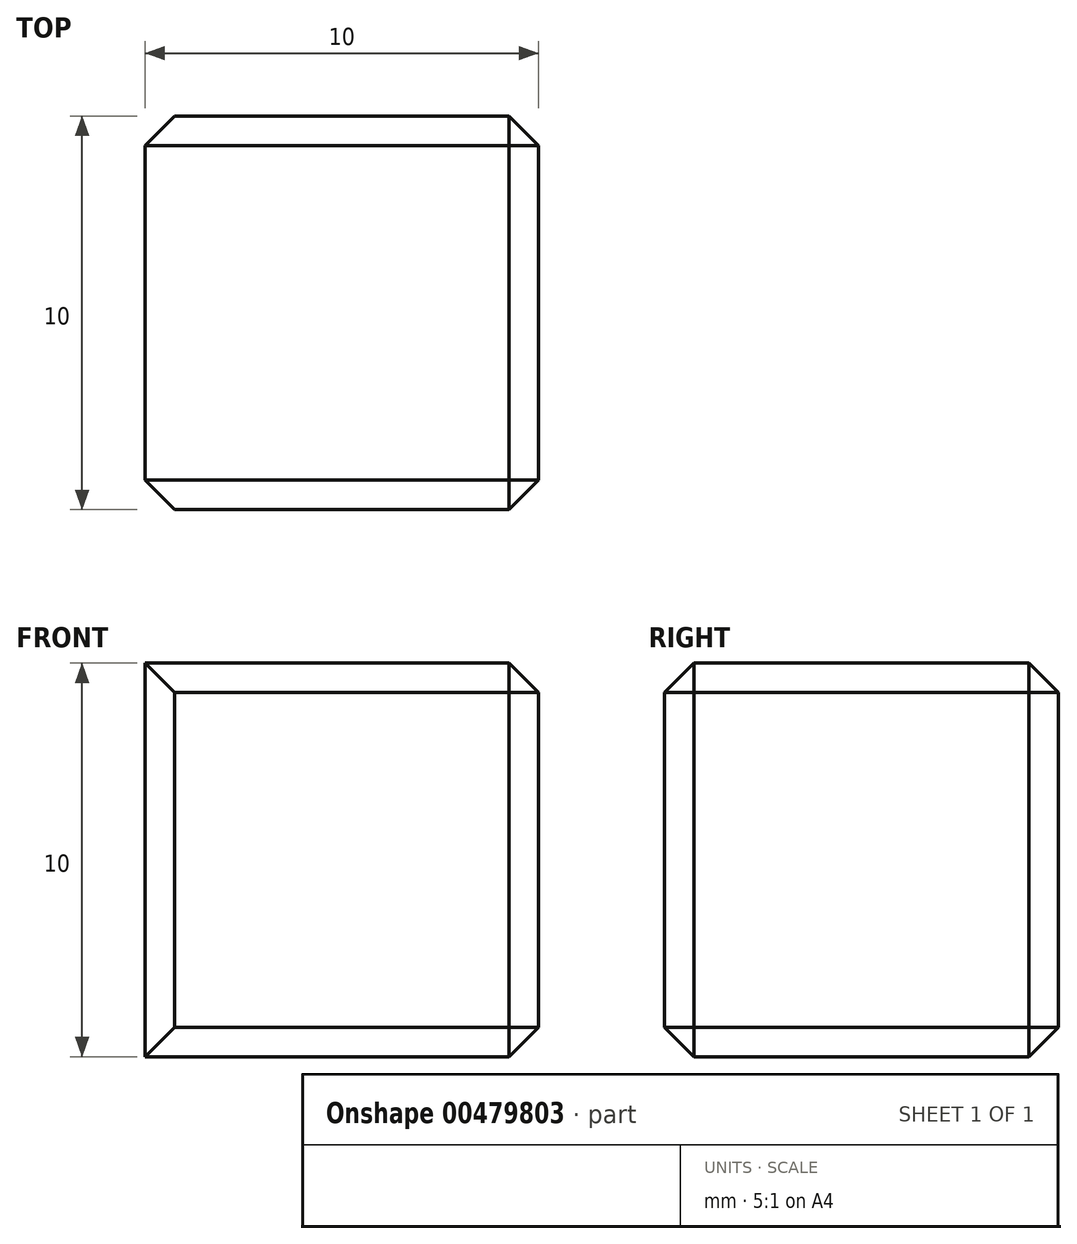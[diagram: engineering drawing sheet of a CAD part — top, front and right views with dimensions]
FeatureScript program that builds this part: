
annotation { "Feature Type Name" : "Feature", "Feature Type Description" : "" }
export const myFeature = defineFeature(function(context is Context, id is Id, definition is map)
    precondition{}
    {
        {
            var Q0;
            Q0=qCreatedBy(makeId("Front.planeOp"),FACE);
            var sketch = newSketch(context, id + "F0", { "sketchPlane" : qUnion([Q0])});
            skLineSegment(sketch, "E0.bottom", {"start": v(5, -5) * mm, "end": v(-5, -5) * mm});
            skLineSegment(sketch, "E0.top", {"start": v(5, 5) * mm, "end": v(-5, 5) * mm});
            skLineSegment(sketch, "E0.left", {"start": v(5, -5) * mm, "end": v(5, 5) * mm});
            skLineSegment(sketch, "E0.right", {"start": v(-5, -5) * mm, "end": v(-5, 5) * mm});
            skPoint(sketch, "E0.middle", {"position": v(0, 0) * mm});
            skSolve(sketch);
        }
        {
            var Q0;
            Q0=makeQuery(id+"F0.imprint","IMPRINT",FACE,{"disambiguationData":[TD([[makeQuery(id+"F0.imprint","IMPRINT",EDGE,{"derivedFrom":sQuery(id+"F0.wireOp",EDGE,"E0.bottom")}),-1.0]])]});
            extrude(context, id + "F1", {"entities" : qUnion([Q0]), "depth" : 10 * mm});
        }
        {
            var Q0;
            Q0=makeQuery(id+"F1.opExtrude","CAP_EDGE",EDGE,{"disambiguationData":[OSD([sQuery(id+"F0.wireOp",EDGE,"E0.top")])],"isStart":true});
            var Q1;
            Q1=makeQuery(id+"F1.opExtrude","CAP_EDGE",EDGE,{"disambiguationData":[OSD([sQuery(id+"F0.wireOp",EDGE,"E0.right")])],"isStart":true});
            var Q2;
            Q2=makeQuery(id+"F1.opExtrude","CAP_EDGE",EDGE,{"disambiguationData":[OSD([sQuery(id+"F0.wireOp",EDGE,"E0.bottom")])],"isStart":true});
            var Q3;
            Q3=makeQuery(id+"F1.opExtrude","CAP_EDGE",EDGE,{"disambiguationData":[OSD([sQuery(id+"F0.wireOp",EDGE,"E0.left")])],"isStart":true});
            var Q4;
            Q4=makeQuery(id+"F1.opExtrude","SWEPT_EDGE",EDGE,{"disambiguationData":[OSD([sQuery(id+"F0.wireOp",EDGE,"E0.bottom"),sQuery(id+"F0.wireOp",EDGE,"E0.left")])]});
            var Q5;
            Q5=makeQuery(id+"F1.opExtrude","SWEPT_EDGE",EDGE,{"disambiguationData":[OSD([sQuery(id+"F0.wireOp",EDGE,"E0.top"),sQuery(id+"F0.wireOp",EDGE,"E0.left")])]});
            var Q6;
            Q6=makeQuery(id+"F1.opExtrude","CAP_EDGE",EDGE,{"disambiguationData":[OSD([sQuery(id+"F0.wireOp",EDGE,"E0.left")])],"isStart":false});
            var Q7;
            Q7=makeQuery(id+"F1.opExtrude","CAP_EDGE",EDGE,{"disambiguationData":[OSD([sQuery(id+"F0.wireOp",EDGE,"E0.bottom")])],"isStart":false});
            var Q8;
            Q8=makeQuery(id+"F1.opExtrude","CAP_EDGE",EDGE,{"disambiguationData":[OSD([sQuery(id+"F0.wireOp",EDGE,"E0.top")])],"isStart":false});
            var Q9;
            Q9=makeQuery(id+"F1.opExtrude","CAP_EDGE",EDGE,{"disambiguationData":[OSD([sQuery(id+"F0.wireOp",EDGE,"E0.right")])],"isStart":false});
            chamfer(context, id + "F2", {"entities" : qUnion([Q0, Q1, Q2, Q3, Q4, Q5, Q6, Q7, Q8, Q9]), "width" : .75 * mm, "tangentPropagation" : true});
        }
    });
